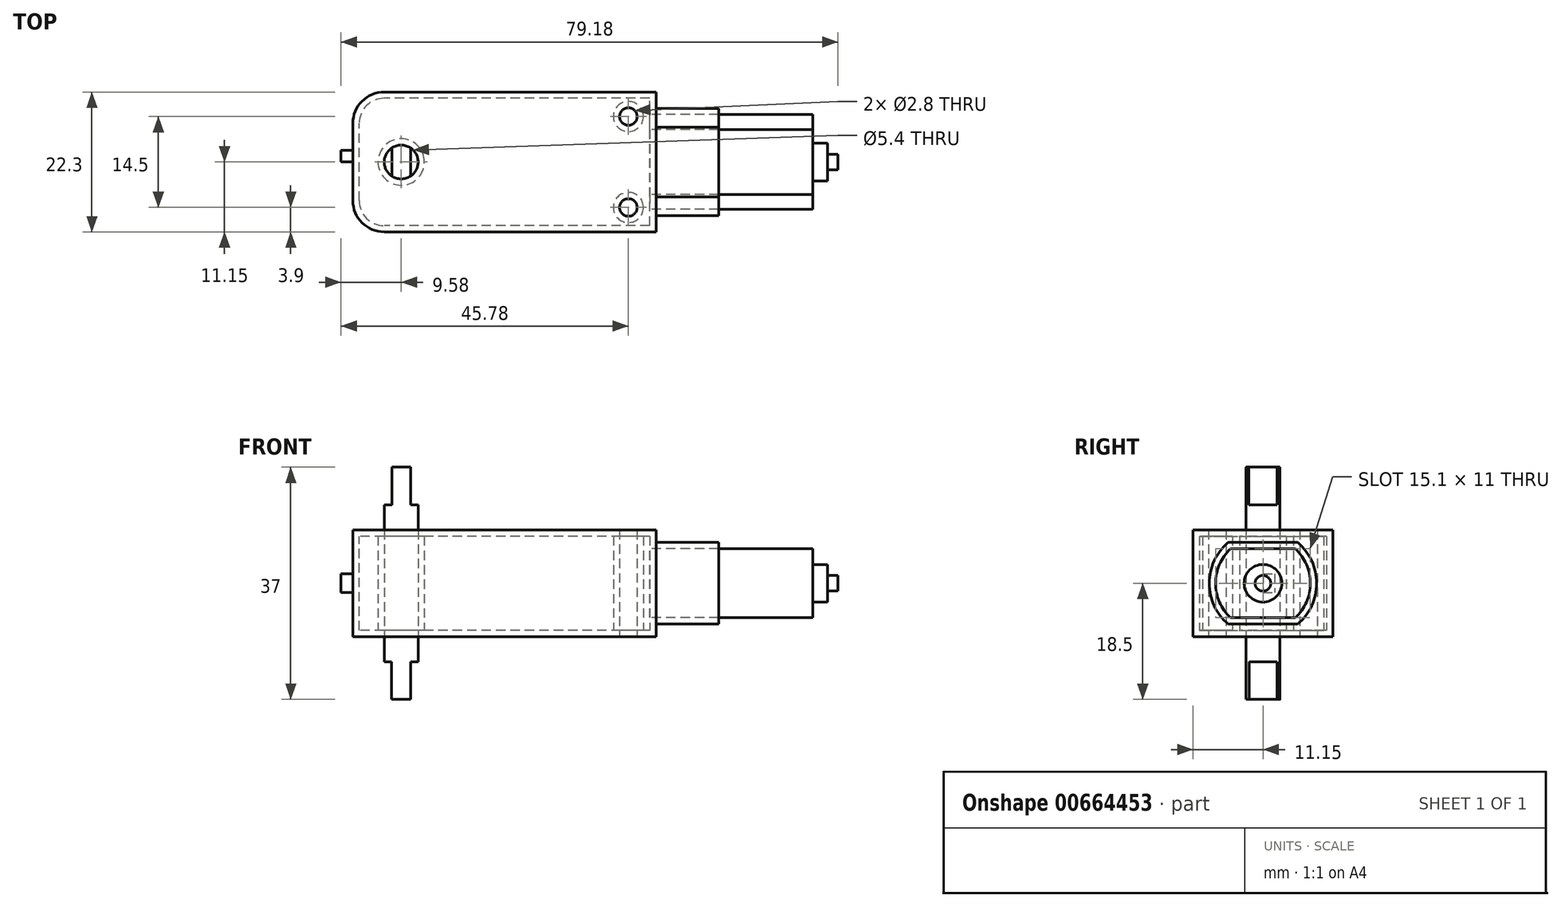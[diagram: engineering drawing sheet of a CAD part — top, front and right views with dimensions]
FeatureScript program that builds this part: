
annotation { "Feature Type Name" : "Feature", "Feature Type Description" : "" }
export const myFeature = defineFeature(function(context is Context, id is Id, definition is map)
    precondition{}
    {
        {
            var Q0;
            Q0=qCreatedBy(makeId("Top.planeOp"),FACE);
            var sketch = newSketch(context, id + "F0", { "sketchPlane" : qUnion([Q0])});
            skLineSegment(sketch, "E0.bottom", {"start": v(24.15, -11.15) * mm, "end": v(-19.15, -11.15) * mm});
            skLineSegment(sketch, "E0.top", {"start": v(24.15, 11.15) * mm, "end": v(-19.15, 11.15) * mm});
            skLineSegment(sketch, "E0.left", {"start": v(24.15, -11.15) * mm, "end": v(24.15, 11.15) * mm});
            skLineSegment(sketch, "E0.right", {"start": v(-24.15, -6.15) * mm, "end": v(-24.15, 6.15) * mm});
            skPoint(sketch, "E0.middle", {"position": v(0, 0) * mm});
            skLineSegment(sketch, "E1", {"start": v(16.16, 11.15) * mm, "end": v(16.16, -11.15) * mm});
            skCircle(sketch, "E2", {"center": v(19.75, 7.25) * mm, "radius": 1.4 * mm});
            skCircle(sketch, "E3", {"center": v(19.75, -7.25) * mm, "radius": 1.4 * mm});
            skCircle(sketch, "E4", {"center": v(-16.45, 0) * mm, "radius": 2.7 * mm});
            skLineSegment(sketch, "E5", {"start": v(-24.15, 1.88) * mm, "end": v(-26.03, 1.88) * mm});
            skLineSegment(sketch, "E6", {"start": v(-26.03, 1.88) * mm, "end": v(-26.03, 0) * mm});
            skLineSegment(sketch, "E7", {"start": v(-26.03, 0) * mm, "end": v(-24.15, 0) * mm});
            skPoint(sketch, "E8.visualSharp", {"position": v(-24.15, 11.15) * mm});
            skArc(sketch, "E8.filletArc", {"start": v(-19.15, 11.15) * mm, "mid": v(-22.69, 9.69) * mm, "end": v(-24.15, 6.15) * mm});
            skPoint(sketch, "E9.visualSharp", {"position": v(-24.15, -11.15) * mm});
            skArc(sketch, "E9.filletArc", {"start": v(-24.15, -6.15) * mm, "mid": v(-22.69, -9.69) * mm, "end": v(-19.15, -11.15) * mm});
            skSolve(sketch);
        }
        {
            var Q0;
            {var subQ0=sQuery(id+"F0.wireOp",EDGE,"E0.left");Q0=makeQuery(id+"F0.imprint","IMPRINT",FACE,{"disambiguationData":[TD([[makeQuery(id+"F0.imprint","IMPRINT",EDGE,{"derivedFrom":subQ0}),1.0]])]});}
            var Q1;
            {var subQ1=sQuery(id+"F0.wireOp",EDGE,"E1");Q1=makeQuery(id+"F0.imprint","IMPRINT",FACE,{"disambiguationData":[TD([[makeQuery(id+"F0.imprint","IMPRINT",EDGE,{"derivedFrom":subQ1}),-1.0]])]});}
            extrude(context, id + "F1", {"entities" : qUnion([Q0, Q1]), "endBound" : BoundingType.SYMMETRIC, "depth" : 17 * mm});
        }
        {
            var Q0;
            {var subQ0=sQuery(id+"F0.wireOp",EDGE,"E5");Q0=makeQuery(id+"F0.imprint","IMPRINT",FACE,{"disambiguationData":[TD([[makeQuery(id+"F0.imprint","IMPRINT",EDGE,{"derivedFrom":subQ0}),1.0]])]});}
            extrude(context, id + "F2", {"entities" : qUnion([Q0]), "operationType" : NewBodyOperationType.ADD, "endBound" : BoundingType.SYMMETRIC, "depth" : 3 * mm});
        }
        {
            var Q0;
            Q0=makeQuery(id+"F0.imprint","IMPRINT",FACE,{"disambiguationData":[TD([[makeQuery(id+"F0.imprint","IMPRINT",EDGE,{"derivedFrom":sQuery(id+"F0.wireOp",EDGE,"E4")}),1.0]])]});
            extrude(context, id + "F3", {"entities" : qUnion([Q0]), "endBound" : BoundingType.SYMMETRIC, "depth" : 37 * mm});
        }
        {
            var Q0;
            Q0=makeQuery(id+"F1.opExtrude","SWEPT_FACE",FACE,{"disambiguationData":[OSD([sQuery(id+"F0.wireOp",EDGE,"E0.left")])]});
            var sketch = newSketch(context, id + "F4", { "sketchPlane" : qUnion([Q0])});
            skArc(sketch, "E10", {"start": v(-5.55, 6.5) * mm, "mid": v(-8.55, 0) * mm, "end": v(-5.55, -6.5) * mm});
            skLineSegment(sketch, "E11.bottom", {"start": v(5.55, -6.5) * mm, "end": v(-5.55, -6.5) * mm});
            skLineSegment(sketch, "E11.top", {"start": v(5.55, 6.5) * mm, "end": v(-5.55, 6.5) * mm});
            skPoint(sketch, "E11.left.end.orphan", {"position": v(10.32, 6.5) * mm});
            skPoint(sketch, "E12.orphan", {"position": v(11.23, -6.5) * mm});
            skPoint(sketch, "E11.right.start.orphan", {"position": v(-10.32, -6.5) * mm});
            skPoint(sketch, "E13.orphan", {"position": v(-11.23, 6.5) * mm});
            skArc(sketch, "E14.trimOffspring", {"start": v(5.55, -6.5) * mm, "mid": v(8.55, 0) * mm, "end": v(5.55, 6.5) * mm});
            skSolve(sketch);
        }
        {
            var Q0;
            Q0=makeQuery(id+"F4.imprint","IMPRINT",FACE,{"disambiguationData":[TD([[makeQuery(id+"F4.imprint","IMPRINT",EDGE,{"derivedFrom":sQuery(id+"F4.wireOp",EDGE,"E10")}),1.0]])]});
            extrude(context, id + "F5", {"entities" : qUnion([Q0]), "operationType" : NewBodyOperationType.ADD, "depth" : 10 * mm});
        }
        {
            var Q0;
            Q0=makeQuery(id+"F5.opExtrude","CAP_FACE",FACE,{"disambiguationData":[OSD([sQuery(id+"F4.wireOp",EDGE,"E10"),sQuery(id+"F4.wireOp",EDGE,"E11.bottom"),sQuery(id+"F4.wireOp",EDGE,"E11.top"),sQuery(id+"F4.wireOp",EDGE,"E14.trimOffspring")])],"isStart":false});
            shell(context, id + "F6", {"entities" : qUnion([Q0]), "thickness" : 1 * mm});
        }
        {
            var Q0;
            Q0=makeQuery(id+"F5.opExtrude","CAP_FACE",FACE,{"disambiguationData":[OSD([sQuery(id+"F4.wireOp",EDGE,"E10"),sQuery(id+"F4.wireOp",EDGE,"E11.bottom"),sQuery(id+"F4.wireOp",EDGE,"E11.top"),sQuery(id+"F4.wireOp",EDGE,"E14.trimOffspring")])],"isStart":false});
            var sketch = newSketch(context, id + "F7", { "sketchPlane" : qUnion([Q0])});
            skArc(sketch, "E15.0", {"start": v(-5.17, 5.5) * mm, "mid": v(-7.55, 0) * mm, "end": v(-5.17, -5.5) * mm});
            skLineSegment(sketch, "E15.1", {"start": v(5.17, 5.5) * mm, "end": v(-5.17, 5.5) * mm});
            skArc(sketch, "E15.2", {"start": v(5.17, -5.5) * mm, "mid": v(7.55, 0) * mm, "end": v(5.17, 5.5) * mm});
            skLineSegment(sketch, "E15.3", {"start": v(5.17, -5.5) * mm, "end": v(-5.17, -5.5) * mm});
            skSolve(sketch);
        }
        {
            var Q0;
            Q0=qSketchRegion(id+"F7",true);
            extrude(context, id + "F8", {"entities" : qUnion([Q0]), "depth" : 15 * mm, "offsetDistance" : 25 * mm});
        }
        {
            var Q0;
            Q0=makeQuery(id+"F8.opExtrude","CAP_FACE",FACE,{"disambiguationData":[OSD([sQuery(id+"F7.wireOp",EDGE,"E15.0"),sQuery(id+"F7.wireOp",EDGE,"E15.1"),sQuery(id+"F7.wireOp",EDGE,"E15.2"),sQuery(id+"F7.wireOp",EDGE,"E15.3")])],"isStart":false});
            var sketch = newSketch(context, id + "F9", { "sketchPlane" : qUnion([Q0])});
            skCircle(sketch, "E16", {"center": v(0, 0) * mm, "radius": 3 * mm});
            skCircle(sketch, "E17", {"center": v(0, 0) * mm, "radius": 1.25 * mm});
            skSolve(sketch);
        }
        {
            var Q0;
            Q0=makeQuery(id+"F9.imprint","IMPRINT",FACE,{"disambiguationData":[TD([[makeQuery(id+"F9.imprint","IMPRINT",EDGE,{"derivedFrom":sQuery(id+"F9.wireOp",EDGE,"E16")}),1.0]])]});
            extrude(context, id + "F10", {"entities" : qUnion([Q0]), "operationType" : NewBodyOperationType.ADD, "depth" : 2.3 * mm});
        }
        {
            var Q0;
            Q0=makeQuery(id+"F10.boolean.opBoolean","SPLIT",FACE,{"disambiguationData":[TD([makeQuery(id+"F10.opExtrude","SWEPT_FACE",FACE,{"disambiguationData":[OSD([sQuery(id+"F9.wireOp",EDGE,"E17")])]})])],"derivedFrom":makeQuery(id+"F8.opExtrude","CAP_FACE",FACE,{"disambiguationData":[OSD([sQuery(id+"F7.wireOp",EDGE,"E15.0"),sQuery(id+"F7.wireOp",EDGE,"E15.1"),sQuery(id+"F7.wireOp",EDGE,"E15.2"),sQuery(id+"F7.wireOp",EDGE,"E15.3")])],"isStart":false})});
            extrude(context, id + "F11", {"entities" : qUnion([Q0]), "operationType" : NewBodyOperationType.ADD, "depth" : 4 * mm, "offsetDistance" : 25 * mm});
        }
        {
            var Q0;
            Q0=makeQuery(id+"F3.opExtrude","CAP_FACE",FACE,{"disambiguationData":[OSD([sQuery(id+"F0.wireOp",EDGE,"E4")])],"isStart":false});
            var sketch = newSketch(context, id + "F12", { "sketchPlane" : qUnion([Q0])});
            skLineSegment(sketch, "E18.bottom", {"start": v(-14.96, -2.25) * mm, "end": v(-17.94, -2.25) * mm});
            skLineSegment(sketch, "E18.top", {"start": v(-14.96, 2.25) * mm, "end": v(-17.94, 2.25) * mm});
            skLineSegment(sketch, "E18.left", {"start": v(-14.96, -2.25) * mm, "end": v(-14.96, 2.25) * mm});
            skLineSegment(sketch, "E18.right", {"start": v(-17.94, -2.25) * mm, "end": v(-17.94, 2.25) * mm});
            skPoint(sketch, "E18.middle", {"position": v(-16.45, 0) * mm});
            skSolve(sketch);
        }
        {
            var Q0;
            {var subQ0=sQuery(id+"F12.wireOp",EDGE,"E18.right");Q0=makeQuery(id+"F12.imprint","IMPRINT",FACE,{"disambiguationData":[TD([[makeQuery(id+"F12.imprint","IMPRINT",EDGE,{"derivedFrom":subQ0}),1.0]])]});}
            var Q1;
            {var subQ0=sQuery(id+"F12.wireOp",EDGE,"E18.left");Q1=makeQuery(id+"F12.imprint","IMPRINT",FACE,{"disambiguationData":[TD([[makeQuery(id+"F12.imprint","IMPRINT",EDGE,{"derivedFrom":subQ0}),-1.0]])]});}
            extrude(context, id + "F13", {"entities" : qUnion([Q0, Q1]), "operationType" : NewBodyOperationType.REMOVE, "oppositeDirection" : true, "depth" : 6 * mm});
        }
        {
            var Q0;
            Q0=makeQuery(id+"F3.opExtrude","CAP_FACE",FACE,{"disambiguationData":[OSD([sQuery(id+"F0.wireOp",EDGE,"E4")])],"isStart":true});
            var sketch = newSketch(context, id + "F14", { "sketchPlane" : qUnion([Q0])});
            skLineSegment(sketch, "E19.bottom", {"start": v(-14.92, 2.23) * mm, "end": v(-17.98, 2.23) * mm});
            skLineSegment(sketch, "E19.top", {"start": v(-14.92, -2.23) * mm, "end": v(-17.98, -2.23) * mm});
            skLineSegment(sketch, "E19.left", {"start": v(-14.92, 2.23) * mm, "end": v(-14.92, -2.23) * mm});
            skLineSegment(sketch, "E19.right", {"start": v(-17.98, 2.23) * mm, "end": v(-17.98, -2.23) * mm});
            skPoint(sketch, "E19.middle", {"position": v(-16.45, 0) * mm});
            skSolve(sketch);
        }
        {
            var Q0;
            {var subQ0=sQuery(id+"F14.wireOp",EDGE,"E19.right");Q0=makeQuery(id+"F14.imprint","IMPRINT",FACE,{"disambiguationData":[TD([[makeQuery(id+"F14.imprint","IMPRINT",EDGE,{"derivedFrom":subQ0}),-1.0]])]});}
            var Q1;
            {var subQ0=sQuery(id+"F14.wireOp",EDGE,"E19.left");Q1=makeQuery(id+"F14.imprint","IMPRINT",FACE,{"disambiguationData":[TD([[makeQuery(id+"F14.imprint","IMPRINT",EDGE,{"derivedFrom":subQ0}),1.0]])]});}
            extrude(context, id + "F15", {"entities" : qUnion([Q0, Q1]), "operationType" : NewBodyOperationType.REMOVE, "oppositeDirection" : true, "depth" : 6 * mm});
        }
    });
